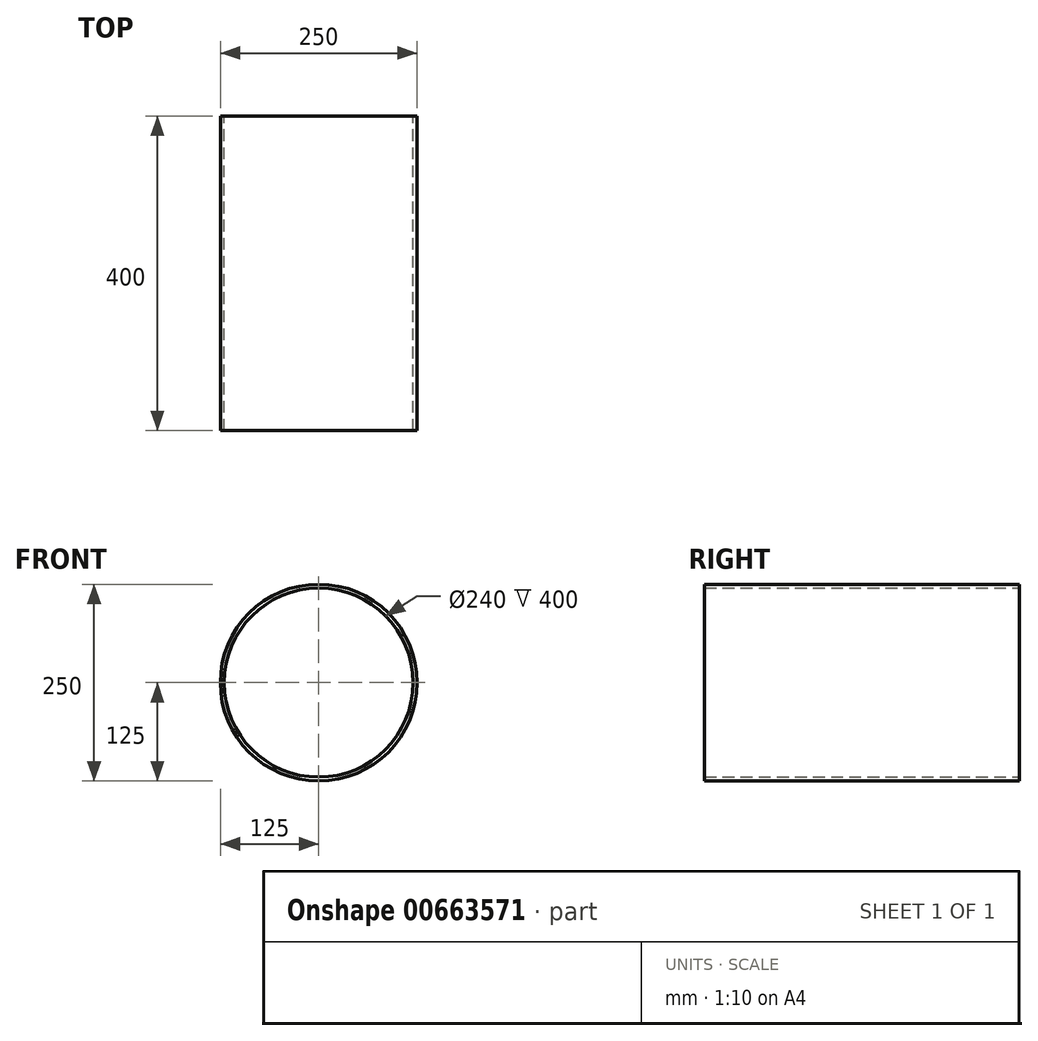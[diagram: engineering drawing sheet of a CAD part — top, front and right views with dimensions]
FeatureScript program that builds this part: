
annotation { "Feature Type Name" : "Feature", "Feature Type Description" : "" }
export const myFeature = defineFeature(function(context is Context, id is Id, definition is map)
    precondition{}
    {
        {
            var Q0;
            Q0=qCreatedBy(makeId("Front.planeOp"),FACE);
            var sketch = newSketch(context, id + "F0", { "sketchPlane" : qUnion([Q0])});
            skCircle(sketch, "E0", {"center": v(0, 0) * mm, "radius": 125 * mm});
            skCircle(sketch, "E1", {"center": v(0, 0) * mm, "radius": 120 * mm});
            skSolve(sketch);
        }
        {
            var Q0;
            Q0=makeQuery(id+"F0.imprint","IMPRINT",FACE,{"disambiguationData":[TD([[makeQuery(id+"F0.imprint","IMPRINT",EDGE,{"derivedFrom":sQuery(id+"F0.wireOp",EDGE,"E0")}),1.0]])]});
            extrude(context, id + "F1", {"entities" : qUnion([Q0]), "depth" : 400 * mm, "offsetDistance" : 25 * mm});
        }
    });
